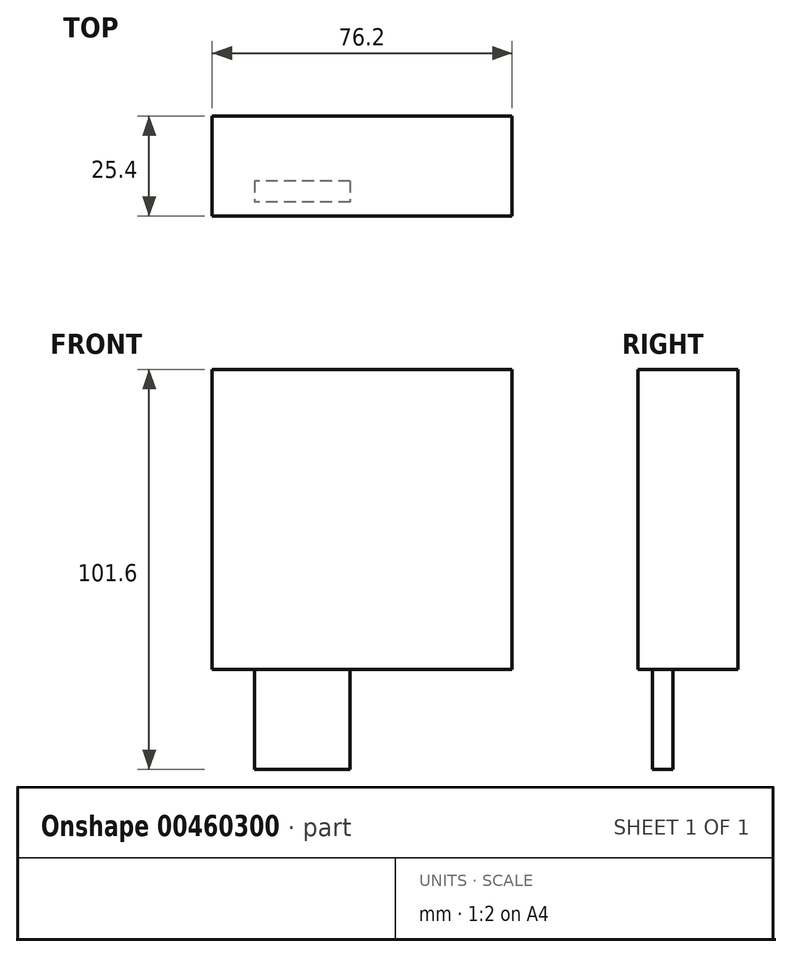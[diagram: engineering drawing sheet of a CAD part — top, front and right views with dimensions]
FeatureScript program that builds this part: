
annotation { "Feature Type Name" : "Feature", "Feature Type Description" : "" }
export const myFeature = defineFeature(function(context is Context, id is Id, definition is map)
    precondition{}
    {
        {
            var Q0;
            Q0=qCreatedBy(makeId("Front.planeOp"),FACE);
            var sketch = newSketch(context, id + "F0", { "sketchPlane" : qUnion([Q0])});
            skLineSegment(sketch, "E0.bottom", {"start": v(-38.1, 38.1) * mm, "end": v(38.1, 38.1) * mm});
            skLineSegment(sketch, "E0.top", {"start": v(-38.1, -38.1) * mm, "end": v(38.1, -38.1) * mm});
            skLineSegment(sketch, "E0.left", {"start": v(-38.1, 38.1) * mm, "end": v(-38.1, -38.1) * mm});
            skLineSegment(sketch, "E0.right", {"start": v(38.1, 38.1) * mm, "end": v(38.1, -38.1) * mm});
            skPoint(sketch, "E0.middle", {"position": v(0, 0) * mm});
            skSolve(sketch);
        }
        {
            var Q0;
            Q0 = qSketchRegion(id + "F0", true);
            extrude(context, id + "F1", {"entities" : qUnion([Q0]), "depth" : 25.4 * mm});
        }
        {
            var Q0;
            Q0=makeQuery(id+"F1.opExtrude","SWEPT_FACE",FACE,{"disambiguationData":[OSD([sQuery(id+"F0.wireOp",EDGE,"E0.top")])]});
            var sketch = newSketch(context, id + "F2", { "sketchPlane" : qUnion([Q0])});
            skLineSegment(sketch, "E1.bottom", {"start": v(-3.03, 16.5) * mm, "end": v(-27.3, 16.5) * mm});
            skLineSegment(sketch, "E1.top", {"start": v(-3.03, 21.8) * mm, "end": v(-27.3, 21.8) * mm});
            skLineSegment(sketch, "E1.left", {"start": v(-3.03, 16.5) * mm, "end": v(-3.03, 21.8) * mm});
            skLineSegment(sketch, "E1.right", {"start": v(-27.3, 16.5) * mm, "end": v(-27.3, 21.8) * mm});
            skPoint(sketch, "E1.middle", {"position": v(-15.17, 19.15) * mm});
            skSolve(sketch);
        }
        {
            var Q0;
            Q0 = qSketchRegion(id + "F2", true);
            extrude(context, id + "F3", {"entities" : qUnion([Q0]), "operationType" : NewBodyOperationType.ADD, "depth" : 25.4 * mm});
        }
    });
